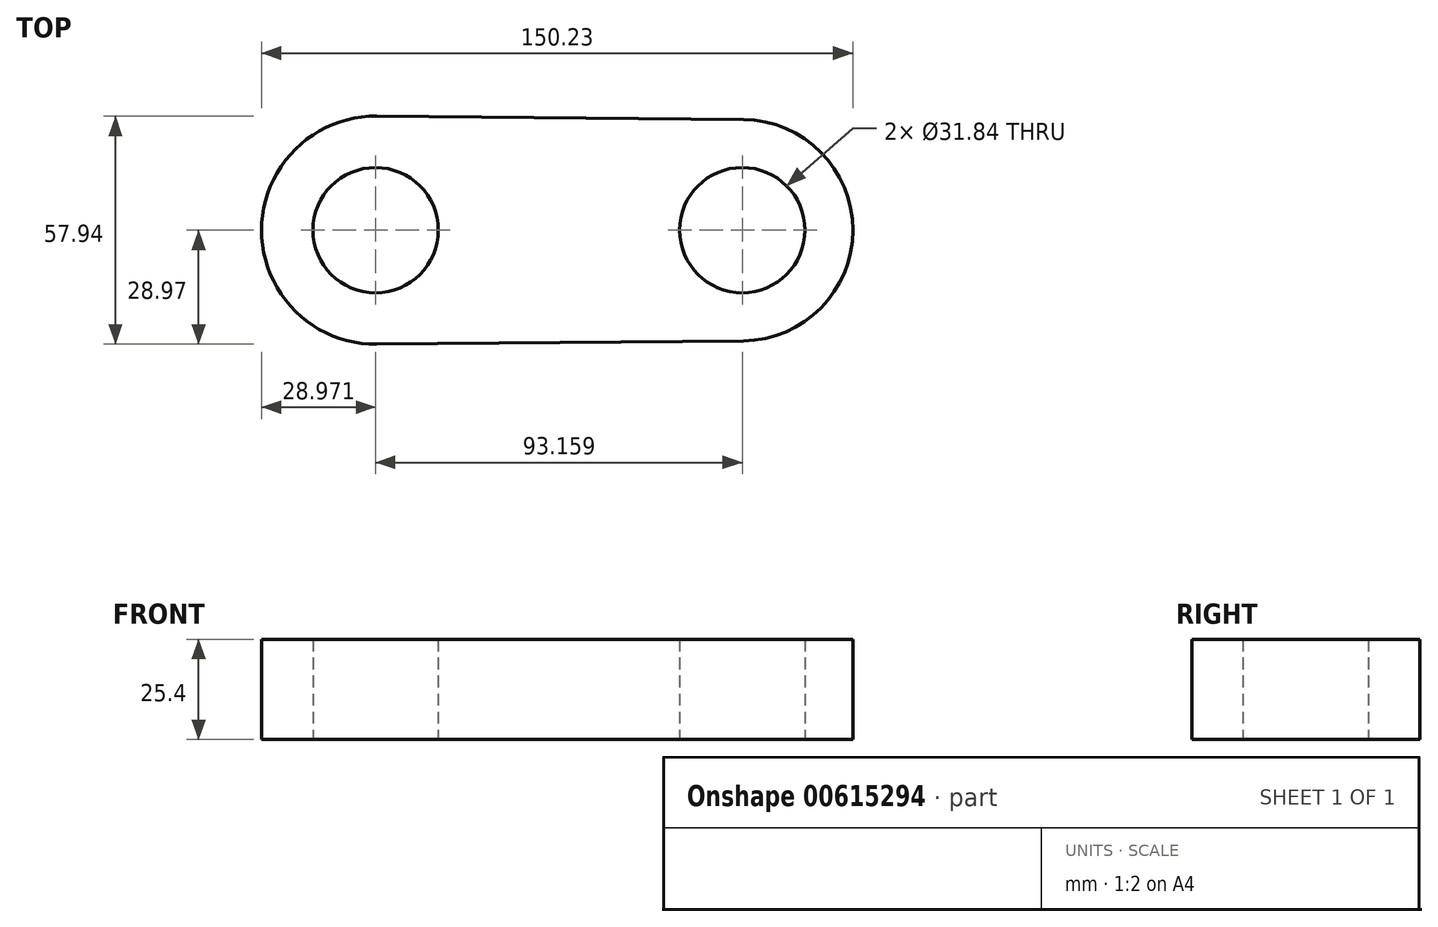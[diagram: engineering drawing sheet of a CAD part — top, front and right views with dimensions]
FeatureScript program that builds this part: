
annotation { "Feature Type Name" : "Feature", "Feature Type Description" : "" }
export const myFeature = defineFeature(function(context is Context, id is Id, definition is map)
    precondition{}
    {
        {
            var Q0;
            Q0=qCreatedBy(makeId("Top.planeOp"),FACE);
            var sketch = newSketch(context, id + "F0", { "sketchPlane" : qUnion([Q0])});
            skCircle(sketch, "E0", {"center": v(-46.58, 0) * mm, "radius": 15.92 * mm});
            skCircle(sketch, "E1", {"center": v(46.58, 0) * mm, "radius": 15.92 * mm});
            skArc(sketch, "E2", {"start": v(-46.3, 28.97) * mm, "mid": v(-75.55, 0) * mm, "end": v(-46.3, -28.97) * mm});
            skArc(sketch, "E3", {"start": v(46.84, -28.1) * mm, "mid": v(74.68, 0) * mm, "end": v(46.84, 28.1) * mm});
            skLineSegment(sketch, "E4", {"start": v(-46.3, 28.97) * mm, "end": v(46.84, 28.1) * mm});
            skLineSegment(sketch, "E5", {"start": v(46.84, -28.1) * mm, "end": v(-46.3, -28.97) * mm});
            skArc(sketch, "E6", {"start": v(-46.3, -28.97) * mm, "mid": v(-17.6, 0) * mm, "end": v(-46.3, 28.97) * mm});
            skSolve(sketch);
        }
        {
            var Q0;
            Q0=makeQuery(id+"F0.imprint","IMPRINT",FACE,{"disambiguationData":[TD([[makeQuery(id+"F0.imprint","IMPRINT",EDGE,{"derivedFrom":sQuery(id+"F0.wireOp",EDGE,"E1")}),-1.0]])]});
            var Q1;
            Q1=makeQuery(id+"F0.imprint","IMPRINT",FACE,{"disambiguationData":[TD([[makeQuery(id+"F0.imprint","IMPRINT",EDGE,{"derivedFrom":sQuery(id+"F0.wireOp",EDGE,"E0")}),-1.0]])]});
            extrude(context, id + "F1", {"entities" : qUnion([Q0, Q1]), "depth" : 25.4 * mm, "offsetDistance" : 25.4 * mm});
        }
    });
